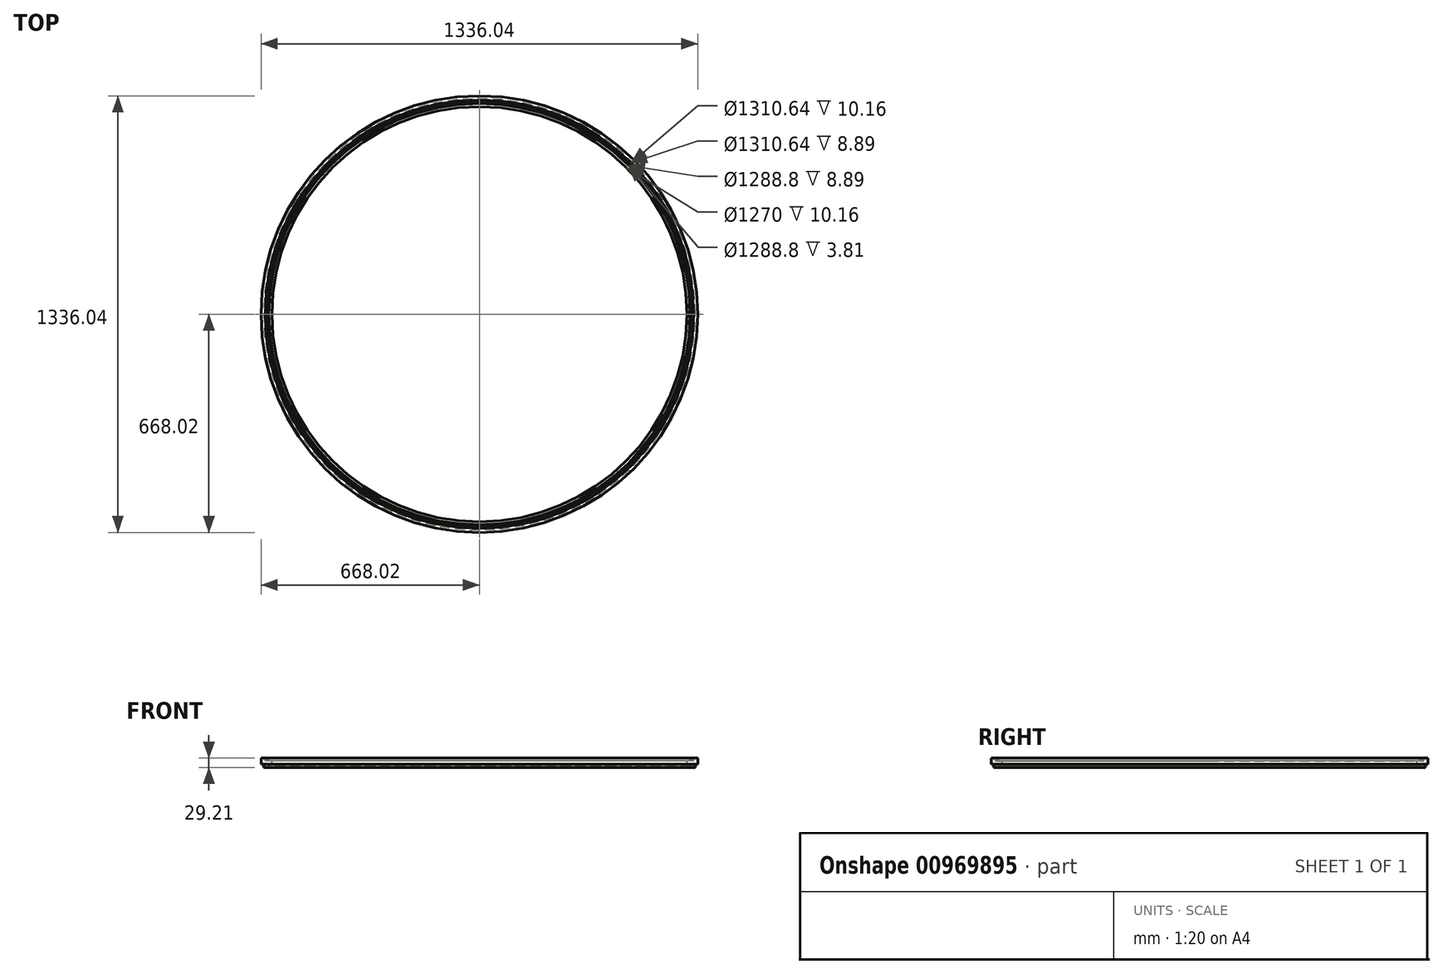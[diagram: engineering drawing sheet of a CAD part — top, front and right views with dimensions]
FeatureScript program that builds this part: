
annotation { "Feature Type Name" : "Feature", "Feature Type Description" : "" }
export const myFeature = defineFeature(function(context is Context, id is Id, definition is map)
    precondition{}
    {
        {
            var Q0;
            Q0=qCreatedBy(makeId("Front.planeOp"),FACE);
            var sketch = newSketch(context, id + "F0", { "sketchPlane" : qUnion([Q0])});
            skLineSegment(sketch, "E0", {"start": v(0, 0) * mm, "end": v(9.4, 0) * mm});
            skLineSegment(sketch, "E1", {"start": v(9.4, -3.81) * mm, "end": v(13.97, -3.81) * mm});
            skLineSegment(sketch, "E2", {"start": v(13.97, -3.81) * mm, "end": v(13.97, 0) * mm});
            skLineSegment(sketch, "E3", {"start": v(13.97, 0) * mm, "end": v(20.32, 0) * mm});
            skLineSegment(sketch, "E4", {"start": v(20.32, 0) * mm, "end": v(20.32, -10.16) * mm});
            skLineSegment(sketch, "E5", {"start": v(20.32, -10.16) * mm, "end": v(25.4, -10.16) * mm});
            skLineSegment(sketch, "E6", {"start": v(25.4, -10.16) * mm, "end": v(25.4, 0) * mm});
            skLineSegment(sketch, "E7", {"start": v(25.4, 0) * mm, "end": v(33.02, 0) * mm});
            skLineSegment(sketch, "E8", {"start": v(33.02, 0) * mm, "end": v(33.02, 19.05) * mm});
            skLineSegment(sketch, "E9", {"start": v(33.02, 19.05) * mm, "end": v(20.32, 19.05) * mm});
            skLineSegment(sketch, "E10", {"start": v(20.32, 19.05) * mm, "end": v(20.32, 10.16) * mm});
            skLineSegment(sketch, "E11", {"start": v(20.32, 10.16) * mm, "end": v(13.97, 10.16) * mm});
            skLineSegment(sketch, "E12", {"start": v(13.97, 10.16) * mm, "end": v(13.97, 19.05) * mm});
            skLineSegment(sketch, "E13", {"start": v(13.97, 19.05) * mm, "end": v(9.4, 19.05) * mm});
            skLineSegment(sketch, "E14", {"start": v(9.4, 19.05) * mm, "end": v(9.4, 10.16) * mm});
            skLineSegment(sketch, "E15", {"start": v(9.4, 10.16) * mm, "end": v(0, 10.16) * mm});
            skLineSegment(sketch, "E16", {"start": v(0, 10.16) * mm, "end": v(0, 0) * mm});
            skLineSegment(sketch, "E17", {"start": v(9.4, 0) * mm, "end": v(9.4, -3.81) * mm});
            skLineSegment(sketch, "E18", {"start": v(-635, 55.87) * mm, "end": v(-635, -57.55) * mm, "construction": true});
            skSolve(sketch);
        }
        {
            var Q0;
            Q0 = qSketchRegion(id + "F0", true);
            var Q1;
            Q1=sQuery(id+"F0.wireOp",EDGE,"E18");
            revolve(context, id + "F1", {"surfaceOperationType" : NewSurfaceOperationType.NEW, "entities" : qUnion([Q0]), "axis" : qUnion([Q1]), "revolveType" : RevolveType.FULL});
        }
    });
